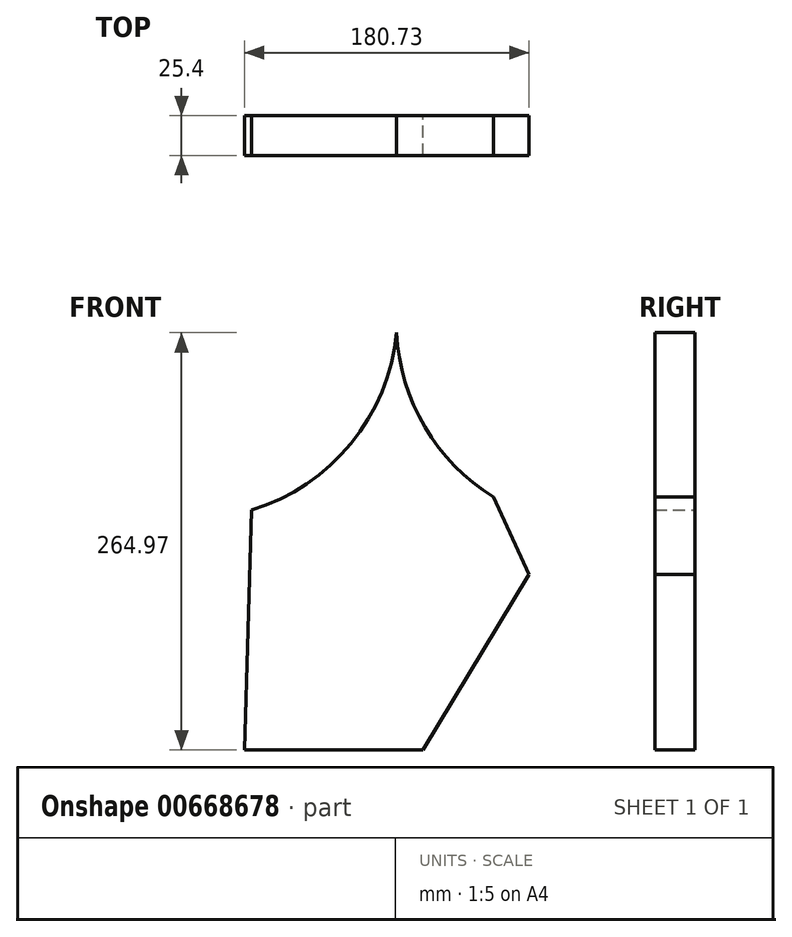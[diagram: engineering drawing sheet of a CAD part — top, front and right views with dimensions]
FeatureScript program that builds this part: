
annotation { "Feature Type Name" : "Feature", "Feature Type Description" : "" }
export const myFeature = defineFeature(function(context is Context, id is Id, definition is map)
    precondition{}
    {
        {
            var Q0;
            Q0=qCreatedBy(makeId("Front.planeOp"),FACE);
            var sketch = newSketch(context, id + "F0", { "sketchPlane" : qUnion([Q0])});
            skLineSegment(sketch, "E0", {"start": v(-109.04, 0) * mm, "end": v(-109.04, 152.4) * mm, "construction": true});
            skLineSegment(sketch, "E1", {"start": v(-109.04, 0) * mm, "end": v(0, 0) * mm});
            skLineSegment(sketch, "E2", {"start": v(0, 0) * mm, "end": v(67.24, 111.46) * mm});
            skLineSegment(sketch, "E3", {"start": v(44.77, 160.54) * mm, "end": v(67.24, 111.46) * mm});
            skArc(sketch, "E4", {"start": v(-109.04, 152.4) * mm, "mid": v(-45.83, 194.64) * mm, "end": v(-16.94, 264.97) * mm});
            skArc(sketch, "E5", {"start": v(-16.3, 264.97) * mm, "mid": v(1.38, 205.24) * mm, "end": v(44.77, 160.54) * mm, "construction": true});
            skLineSegment(sketch, "E6", {"start": v(-109.04, 152.4) * mm, "end": v(-113.49, 0) * mm});
            skLineSegment(sketch, "E7", {"start": v(-113.49, 0) * mm, "end": v(-109.04, 0) * mm});
            skLineSegment(sketch, "E8", {"start": v(-16.94, 264.97) * mm, "end": v(-16.3, 264.97) * mm});
            skPoint(sketch, "E9.orphan", {"position": v(-16.4, 274.08) * mm});
            skArc(sketch, "E10", {"start": v(-16.94, 264.97) * mm, "mid": v(1.02, 205.13) * mm, "end": v(44.77, 160.54) * mm});
            skSolve(sketch);
        }
        {
            var Q0;
            Q0 = qSketchRegion(id + "F0", true);
            extrude(context, id + "F1", {"entities" : qUnion([Q0]), "depth" : 25.4 * mm, "offsetDistance" : 25.4 * mm});
        }
    });
